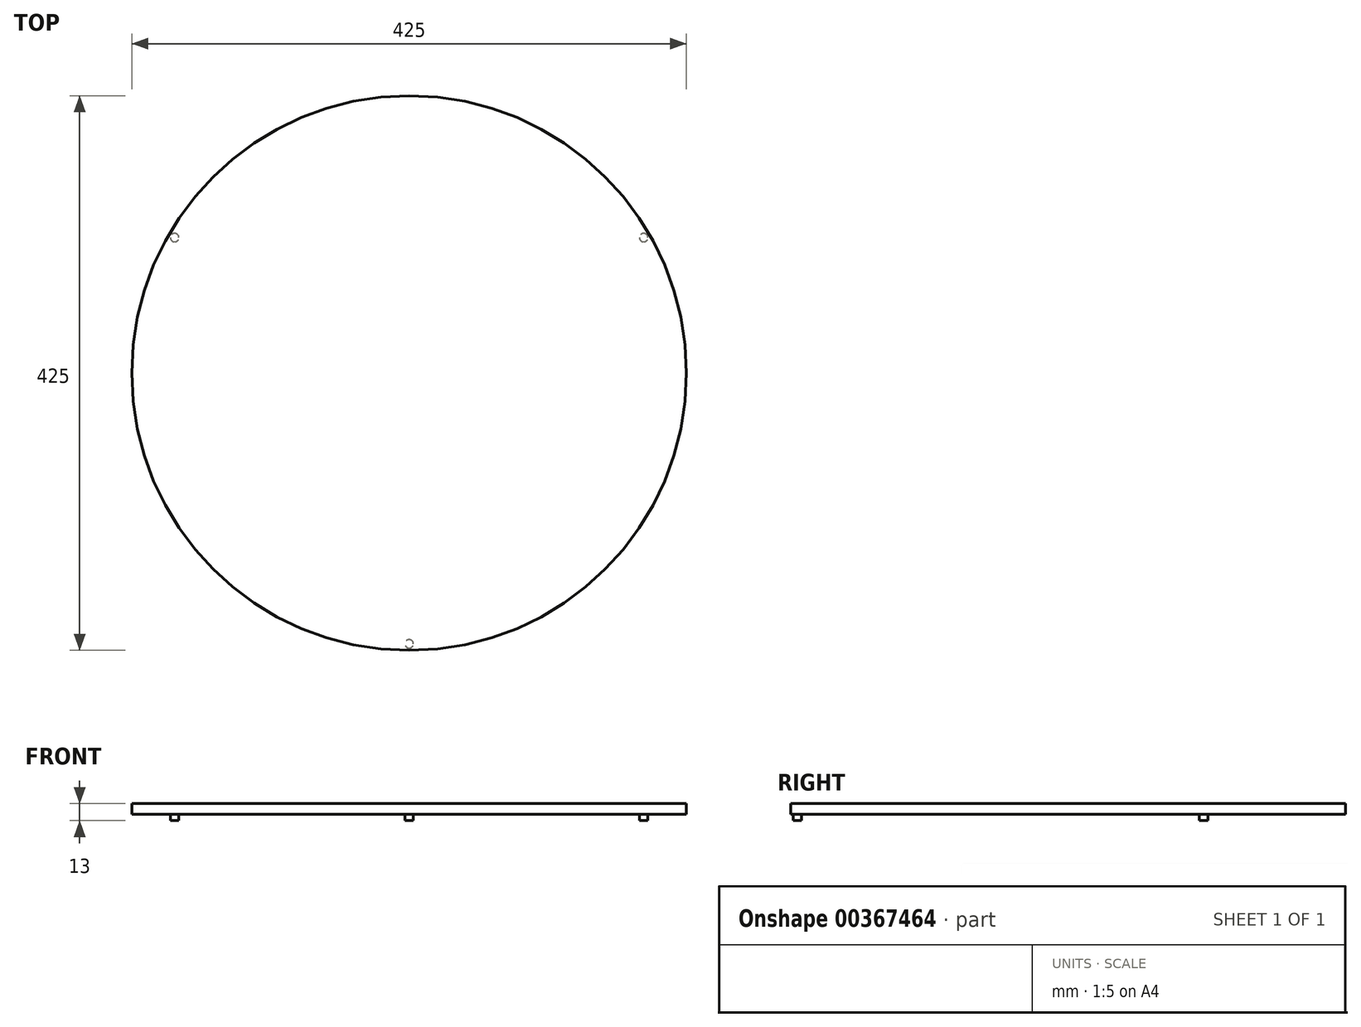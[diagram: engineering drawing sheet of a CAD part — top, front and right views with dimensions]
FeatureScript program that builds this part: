
annotation { "Feature Type Name" : "Feature", "Feature Type Description" : "" }
export const myFeature = defineFeature(function(context is Context, id is Id, definition is map)
    precondition{}
    {
        {
            var Q0;
            Q0=qCreatedBy(makeId("Top.planeOp"),FACE);
            var sketch = newSketch(context, id + "F0", { "sketchPlane" : qUnion([Q0])});
            skCircle(sketch, "E0", {"center": v(0, 0) * mm, "radius": 212.5 * mm});
            skSolve(sketch);
        }
        {
            var Q0;
            Q0=qSketchRegion(id+"F0",true);
            extrude(context, id + "F1", {"entities" : qUnion([Q0]), "depth" : 8 * mm});
        }
        {
            var Q0;
            Q0=makeQuery(id+"F1.opExtrude","CAP_FACE",FACE,{"disambiguationData":[OSD([sQuery(id+"F0.wireOp",EDGE,"E0")])],"isStart":true});
            var sketch = newSketch(context, id + "F2", { "sketchPlane" : qUnion([Q0])});
            skCircle(sketch, "E1", {"center": v(0, 207.5) * mm, "radius": 3.25 * mm});
            skPoint(sketch, "E2.center", {"position": v(0, 0) * mm});
            skCircle(sketch, "E3.1.0", {"center": v(-179.7, -103.75) * mm, "radius": 3.25 * mm});
            skCircle(sketch, "E3.2.0", {"center": v(179.7, -103.75) * mm, "radius": 3.25 * mm});
            skSolve(sketch);
        }
        {
            var Q0;
            Q0=qSketchRegion(id+"F2",true);
            extrude(context, id + "F3", {"entities" : qUnion([Q0]), "operationType" : NewBodyOperationType.ADD, "depth" : 5 * mm});
        }
    });
